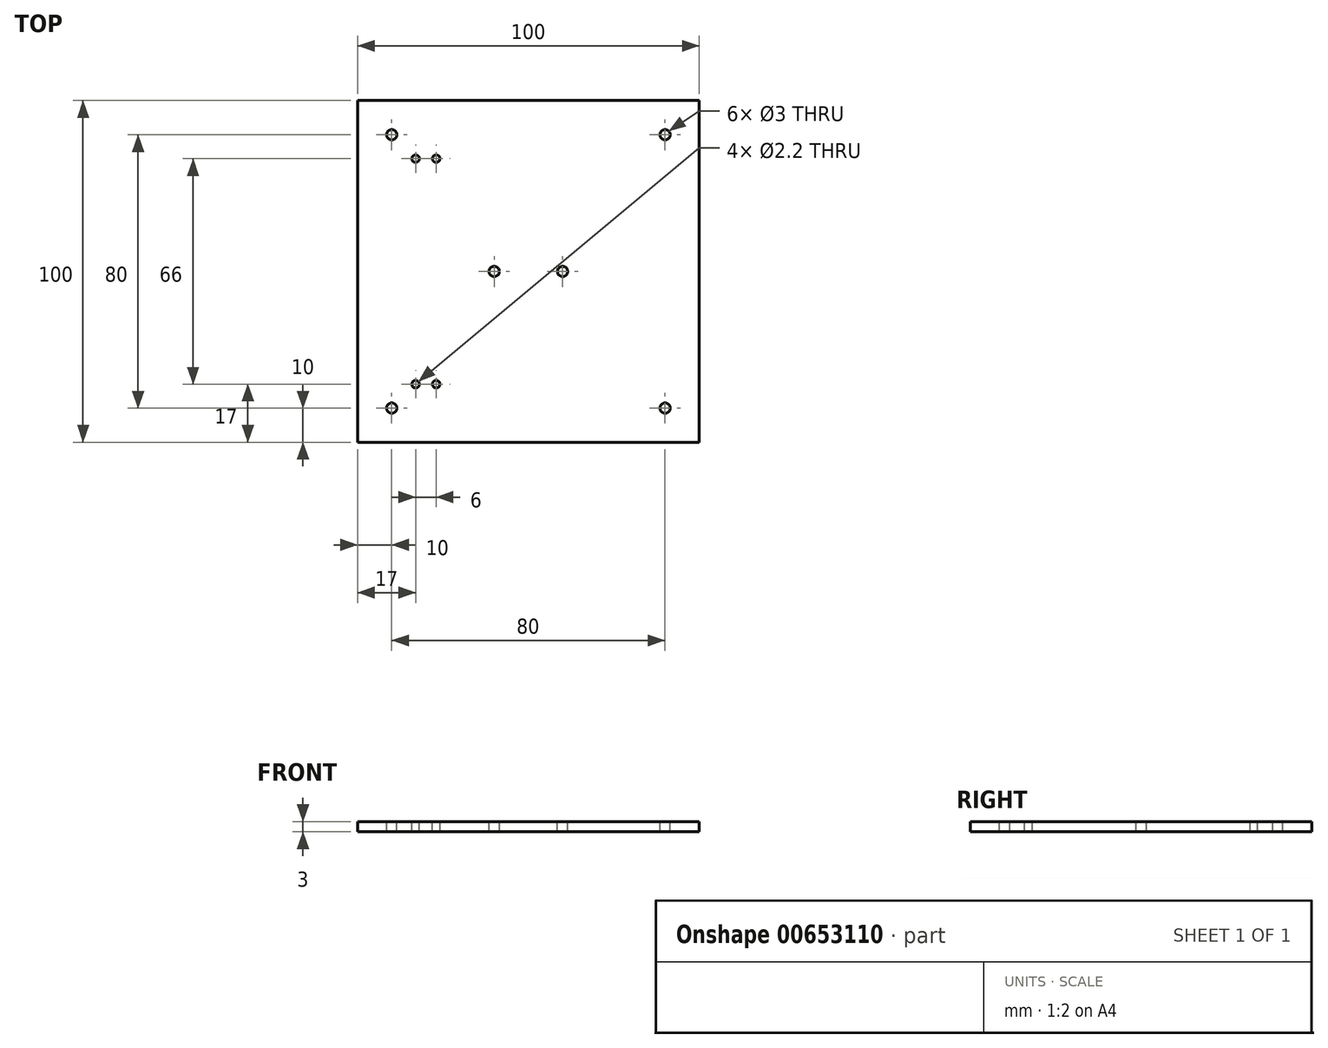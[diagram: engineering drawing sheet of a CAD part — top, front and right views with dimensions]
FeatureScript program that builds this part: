
annotation { "Feature Type Name" : "Feature", "Feature Type Description" : "" }
export const myFeature = defineFeature(function(context is Context, id is Id, definition is map)
    precondition{}
    {
        {
            var Q0;
            Q0=qCreatedBy(makeId("Top.planeOp"),FACE);
            var sketch = newSketch(context, id + "F0", { "sketchPlane" : qUnion([Q0])});
            skLineSegment(sketch, "E0.bottom", {"start": v(0, 0) * mm, "end": v(100, 0) * mm});
            skLineSegment(sketch, "E0.top", {"start": v(0, 100) * mm, "end": v(100, 100) * mm});
            skLineSegment(sketch, "E0.left", {"start": v(0, 0) * mm, "end": v(0, 100) * mm});
            skLineSegment(sketch, "E0.right", {"start": v(100, 0) * mm, "end": v(100, 100) * mm});
            skSolve(sketch);
        }
        {
            var Q0;
            Q0 = qSketchRegion(id + "F0", true);
            extrude(context, id + "F1", {"entities" : qUnion([Q0]), "depth" : 3 * mm, "offsetDistance" : 25 * mm});
        }
        {
            var Q0;
            Q0=makeQuery(id+"F1.opExtrude","CAP_FACE",FACE,{"disambiguationData":[OSD([sQuery(id+"F0.wireOp",EDGE,"E0.bottom"),sQuery(id+"F0.wireOp",EDGE,"E0.top"),sQuery(id+"F0.wireOp",EDGE,"E0.left"),sQuery(id+"F0.wireOp",EDGE,"E0.right")])],"isStart":false});
            var sketch = newSketch(context, id + "F2", { "sketchPlane" : qUnion([Q0])});
            skLineSegment(sketch, "E1", {"start": v(-11.88, 50) * mm, "end": v(119.29, 50) * mm, "construction": true});
            skLineSegment(sketch, "E2", {"start": v(50, 100.47) * mm, "end": v(50, -1.76) * mm, "construction": true});
            skCircle(sketch, "E3", {"center": v(10, 90) * mm, "radius": 1.5 * mm});
            skCircle(sketch, "E4", {"center": v(90, 90) * mm, "radius": 1.5 * mm});
            skCircle(sketch, "E5", {"center": v(90, 10) * mm, "radius": 1.5 * mm});
            skCircle(sketch, "E6", {"center": v(10, 10) * mm, "radius": 1.5 * mm});
            skSolve(sketch);
        }
        {
            var Q0;
            Q0 = qSketchRegion(id + "F2", true);
            extrude(context, id + "F3", {"entities" : qUnion([Q0]), "operationType" : NewBodyOperationType.REMOVE, "endBound" : BoundingType.THROUGH_ALL, "oppositeDirection" : true, "depth" : 25 * mm, "offsetDistance" : 25 * mm});
        }
        {
            var Q0;
            Q0=makeQuery(id+"F1.opExtrude","CAP_FACE",FACE,{"disambiguationData":[OSD([sQuery(id+"F0.wireOp",EDGE,"E0.bottom"),sQuery(id+"F0.wireOp",EDGE,"E0.top"),sQuery(id+"F0.wireOp",EDGE,"E0.left"),sQuery(id+"F0.wireOp",EDGE,"E0.right")])],"isStart":false});
            var sketch = newSketch(context, id + "F4", { "sketchPlane" : qUnion([Q0])});
            skLineSegment(sketch, "E7", {"start": v(20, 65.75) * mm, "end": v(20, 31.39) * mm, "construction": true});
            skLineSegment(sketch, "E8", {"start": v(31.33, 50) * mm, "end": v(67.7, 50) * mm, "construction": true});
            skCircle(sketch, "E9", {"center": v(17, 83) * mm, "radius": 1.1 * mm});
            skCircle(sketch, "E10", {"center": v(23, 83) * mm, "radius": 1.1 * mm});
            skCircle(sketch, "E11", {"center": v(17, 17) * mm, "radius": 1.1 * mm});
            skCircle(sketch, "E12", {"center": v(23, 17) * mm, "radius": 1.1 * mm});
            skSolve(sketch);
        }
        {
            var Q0;
            Q0 = qSketchRegion(id + "F4", true);
            extrude(context, id + "F5", {"entities" : qUnion([Q0]), "operationType" : NewBodyOperationType.REMOVE, "endBound" : BoundingType.THROUGH_ALL, "oppositeDirection" : true, "depth" : 25 * mm, "offsetDistance" : 25 * mm});
        }
        {
            var Q0;
            Q0=makeQuery(id+"F1.opExtrude","CAP_FACE",FACE,{"disambiguationData":[OSD([sQuery(id+"F0.wireOp",EDGE,"E0.bottom"),sQuery(id+"F0.wireOp",EDGE,"E0.top"),sQuery(id+"F0.wireOp",EDGE,"E0.left"),sQuery(id+"F0.wireOp",EDGE,"E0.right")])],"isStart":false});
            var sketch = newSketch(context, id + "F6", { "sketchPlane" : qUnion([Q0])});
            skLineSegment(sketch, "E13", {"start": v(-14.76, 50) * mm, "end": v(118.8, 50) * mm, "construction": true});
            skCircle(sketch, "E14", {"center": v(40, 50) * mm, "radius": 1.5 * mm});
            skCircle(sketch, "E15", {"center": v(60, 50) * mm, "radius": 1.5 * mm});
            skSolve(sketch);
        }
        {
            var Q0;
            Q0 = qSketchRegion(id + "F6", true);
            extrude(context, id + "F7", {"entities" : qUnion([Q0]), "operationType" : NewBodyOperationType.REMOVE, "endBound" : BoundingType.THROUGH_ALL, "oppositeDirection" : true, "depth" : 25 * mm, "offsetDistance" : 25 * mm});
        }
    });
